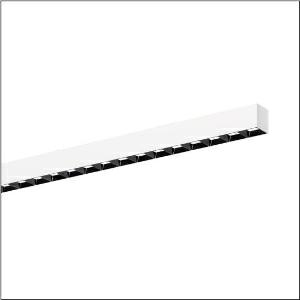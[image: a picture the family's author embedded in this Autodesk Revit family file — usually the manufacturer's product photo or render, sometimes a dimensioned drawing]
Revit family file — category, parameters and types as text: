
# Revit family: silica_r__21_51mx24da44wb_4eb4
name_source: partatom
category: Lighting Fixtures
units: mm (PartAtom-declared; Revit-internal decimal feet)

## family parameters
Cut with Voids When Loaded = No
Host = Face
Light Source = No
Part Type = Normal
Room Calculation Point = No
Round Connector Dimension = Use Diameter
Shared = No

## types (1)
- --- (1 x LED, 4320 lm, 30 W, 4000K)
    Apparent Load = 30 VA
    CIE Flux Codes = 74 94 99 100 100
    Color Rendering = 80
    Color Temperature = 4000K
    Default Elevation = 1800 mm
    Description = Silica® 21, office luminaire, primary light control with darklight reflector, of PMMA, black, CAT 2 (L<= 3000cd/m²), light emission: direct distribution, primary light characteristic: asymmetric, installation type: surface-mounted, LED, rated luminous flux: 4.320lm, luminous efficacy: 144lm/W, light colour: 840, colour temperature: 4000K, with terminal, 3+2-pole, max. 2.5mm², mains connection: 220..240V, AC, 50/60Hz, rated input power: 30W, luminaire housing, of aluminium, traffic white (RAL 9016), length: 1.204mm, width: 53mm, height: 53mm, protection rating (complete): IP20, insulation class (complete): insulation class I (protective earthing), certification: CE, permissible operating ambient temperature: 0..+35°C, standard: EN 50419, packaging unit: 1 piece
    Height = 0 mm  [stored 0 ft]
    Lamp = 1 x LED
    Lamp Light Flux = 4320 lm
    Lamp Power = 30 W
    Lamp count = 1
    Length = 1204 mm
    Luminous efficacy = 144 lm/W
    Manufacturer = Siteco
    ModVariant = No
    Model = 51MX24DA44WB
    Mounting Place = Ceiling
    Mounting Type = Recessed
    Number of Poles = 1
    OnlyDefault = Yes
    Power Factor = 1
    Product Name = Silica® 21
    Product group = office luminaire | ceiling recessed
    ProductGroupID = 400
    Protection Class = Protection class I
    Protection Degree = IP 20
    RLX_Detail_Level = 1
    RLX_Emergency_Light_Flux = 0 lm
    RLX_Emergency_Type = 0
    RLX_Emergency_Type_DB = No
    RlxData = <blob elided: 41645 chars, md5=f54ed8c2>
    Socket = socket
    Standby Power = 0 W
    System Light Flux = 4320 lm
    System Power = 30 W
    Type Comments = factory setting: luminous flux: 100 % | dim-lin: 254 | 418 mA
    Type Image = l_1335873.jpg
    URL = http://relux.com
    VarID = @adj_092789
    Voltage = 0 V
    Weight = 0.00 kg
    Width = 53 mm

note: [stored X ft] marks values corroborated as IEEE doubles in the binary element streams (Revit-internal decimal feet)

## geometry (parser evidence)
native form markers: Blend x4, Sweep x10
no freeform markers — native parametric forms only
